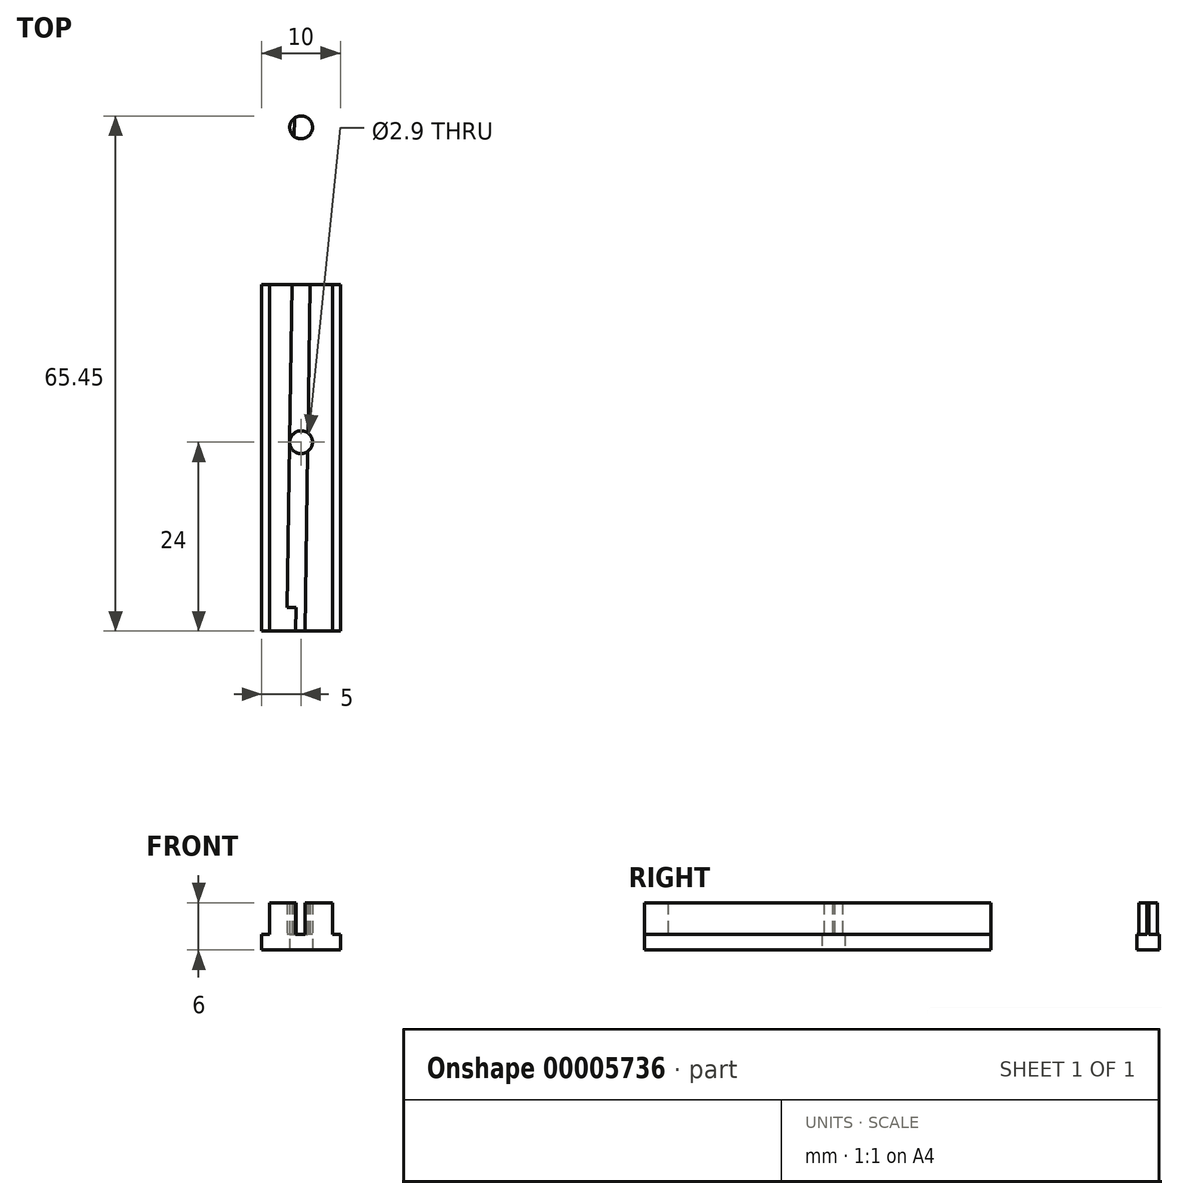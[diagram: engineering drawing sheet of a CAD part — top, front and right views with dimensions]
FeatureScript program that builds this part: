
annotation { "Feature Type Name" : "Feature", "Feature Type Description" : "" }
export const myFeature = defineFeature(function(context is Context, id is Id, definition is map)
    precondition{}
    {
        {
            var Q0;
            Q0=qCreatedBy(makeId("Top.planeOp"),FACE);
            var sketch = newSketch(context, id + "F0", { "sketchPlane" : qUnion([Q0])});
            skLineSegment(sketch, "E0.bottom", {"start": v(-5, 44) * mm, "end": v(5, 44) * mm});
            skLineSegment(sketch, "E0.top", {"start": v(-5, -44) * mm, "end": v(5, -44) * mm});
            skLineSegment(sketch, "E0.left", {"start": v(-5, 44) * mm, "end": v(-5, -44) * mm});
            skLineSegment(sketch, "E0.right", {"start": v(5, 44) * mm, "end": v(5, -44) * mm});
            skPoint(sketch, "E0.middle", {"position": v(0, 0) * mm});
            skLineSegment(sketch, "E1", {"start": v(0, 44) * mm, "end": v(0, -44) * mm, "construction": true});
            skLineSegment(sketch, "E2", {"start": v(1.8, 44) * mm, "end": v(0.5, -44) * mm});
            skLineSegment(sketch, "E3", {"start": v(-0.5, 44) * mm, "end": v(-1.8, -44) * mm});
            skLineSegment(sketch, "E4", {"start": v(0.7, 44) * mm, "end": v(0.66, 41) * mm});
            skLineSegment(sketch, "E5", {"start": v(0.66, 41) * mm, "end": v(1.76, 40.98) * mm});
            skLineSegment(sketch, "E6.1.0", {"start": v(-0.7, -44) * mm, "end": v(-0.66, -41) * mm});
            skLineSegment(sketch, "E6.1.1", {"start": v(-0.66, -41) * mm, "end": v(-1.76, -40.98) * mm});
            skLineSegment(sketch, "E7", {"start": v(4, 44) * mm, "end": v(4, -44) * mm});
            skLineSegment(sketch, "E8.MirrorCS", {"start": v(-4, 44) * mm, "end": v(-4, -44) * mm});
            skLineSegment(sketch, "E9.bottom", {"start": v(-4, 16.82) * mm, "end": v(4, 16.82) * mm});
            skLineSegment(sketch, "E9.top", {"start": v(-4, -16.82) * mm, "end": v(4, -16.82) * mm});
            skLineSegment(sketch, "E9.left", {"start": v(-4, 16.82) * mm, "end": v(-4, -16.82) * mm});
            skLineSegment(sketch, "E9.right", {"start": v(4, 16.82) * mm, "end": v(4, -16.82) * mm});
            skSolve(sketch);
        }
        {
            var Q0;
            {var subQ4=sQuery(id+"F0.wireOp",EDGE,"E0.left");Q0=makeQuery(id+"F0.imprint","IMPRINT",FACE,{"disambiguationData":[TD([[makeQuery(id+"F0.imprint","IMPRINT",EDGE,{"derivedFrom":subQ4}),1.0]])]});}
            var Q1;
            {var subQ4=sQuery(id+"F0.wireOp",EDGE,"E0.right");Q1=makeQuery(id+"F0.imprint","IMPRINT",FACE,{"disambiguationData":[TD([[makeQuery(id+"F0.imprint","IMPRINT",EDGE,{"derivedFrom":subQ4}),-1.0]])]});}
            var Q2;
            {var subQ3=sQuery(id+"F0.wireOp",EDGE,"E6.1.0");Q2=makeQuery(id+"F0.imprint","IMPRINT",FACE,{"disambiguationData":[TD([[makeQuery(id+"F0.imprint","IMPRINT",EDGE,{"derivedFrom":subQ3}),1.0]])]});}
            var Q3;
            {var subQ3=sQuery(id+"F0.wireOp",EDGE,"E4");Q3=makeQuery(id+"F0.imprint","IMPRINT",FACE,{"disambiguationData":[TD([[makeQuery(id+"F0.imprint","IMPRINT",EDGE,{"derivedFrom":subQ3}),1.0]])]});}
            var Q4;
            {var subQ6=sQuery(id+"F0.wireOp",EDGE,"E7");Q4=makeQuery(id+"F0.imprint","IMPRINT",FACE,{"disambiguationData":[TD([[makeQuery(id+"F0.imprint","IMPRINT",EDGE,{"derivedFrom":subQ6}),-1.0]])]});}
            var Q5;
            {var subQ3=sQuery(id+"F0.wireOp",EDGE,"E8.MirrorCS");Q5=makeQuery(id+"F0.imprint","IMPRINT",FACE,{"disambiguationData":[TD([[makeQuery(id+"F0.imprint","IMPRINT",EDGE,{"derivedFrom":subQ3}),1.0]])]});}
            var Q6;
            {var subQ1=sQuery(id+"F0.wireOp",EDGE,"E0.top");var subQ5=sQuery(id+"F0.wireOp",EDGE,"E3");var subQ7=makeQuery(id+"F0.imprint","INTERSECT",VERTEX,{"derivedFrom":[subQ1,subQ5]});Q6=makeQuery(id+"F0.imprint","IMPRINT",FACE,{"disambiguationData":[TD([[makeQuery(id+"F0.imprint","IMPRINT",EDGE,{"disambiguationData":[TD([[subQ7,1.0]])],"derivedFrom":subQ1}),1.0]])]});}
            var Q7;
            {var subQ5=sQuery(id+"F0.wireOp",EDGE,"E9.left");Q7=makeQuery(id+"F0.imprint","IMPRINT",FACE,{"disambiguationData":[TD([[makeQuery(id+"F0.imprint","IMPRINT",EDGE,{"derivedFrom":subQ5}),1.0]])]});}
            var Q8;
            {var subQ0=sQuery(id+"F0.wireOp",EDGE,"E9.bottom");var subQ1=sQuery(id+"F0.wireOp",EDGE,"E2");var subQ2=makeQuery(id+"F0.imprint","INTERSECT",VERTEX,{"derivedFrom":[subQ1,subQ0]});Q8=makeQuery(id+"F0.imprint","IMPRINT",FACE,{"disambiguationData":[TD([[makeQuery(id+"F0.imprint","IMPRINT",EDGE,{"disambiguationData":[TD([[subQ2,-1.0]])],"derivedFrom":subQ1}),-1.0]])]});}
            var Q9;
            {var subQ5=sQuery(id+"F0.wireOp",EDGE,"E9.right");Q9=makeQuery(id+"F0.imprint","IMPRINT",FACE,{"disambiguationData":[TD([[makeQuery(id+"F0.imprint","IMPRINT",EDGE,{"derivedFrom":subQ5}),-1.0]])]});}
            var Q10;
            {var subQ1=sQuery(id+"F0.wireOp",EDGE,"E0.bottom");var subQ5=sQuery(id+"F0.wireOp",EDGE,"E2");var subQ8=makeQuery(id+"F0.imprint","INTERSECT",VERTEX,{"derivedFrom":[subQ1,subQ5]});Q10=makeQuery(id+"F0.imprint","IMPRINT",FACE,{"disambiguationData":[TD([[makeQuery(id+"F0.imprint","IMPRINT",EDGE,{"disambiguationData":[TD([[subQ8,-1.0]])],"derivedFrom":subQ1}),-1.0]])]});}
            var Q11;
            {var subQ0=sQuery(id+"F0.wireOp",EDGE,"E4");Q11=makeQuery(id+"F0.imprint","IMPRINT",FACE,{"disambiguationData":[TD([[makeQuery(id+"F0.imprint","IMPRINT",EDGE,{"derivedFrom":subQ0}),-1.0]])]});}
            var Q12;
            {var subQ8=sQuery(id+"F0.wireOp",EDGE,"E6.1.0");Q12=makeQuery(id+"F0.imprint","IMPRINT",FACE,{"disambiguationData":[TD([[makeQuery(id+"F0.imprint","IMPRINT",EDGE,{"derivedFrom":subQ8}),-1.0]])]});}
            extrude(context, id + "F1", {"entities" : qUnion([Q0, Q1, Q2, Q3, Q4, Q5, Q6, Q7, Q8, Q9, Q10, Q11, Q12]), "oppositeDirection" : true, "depth" : 2 * mm});
        }
        {
            var Q0;
            {var subQ3=sQuery(id+"F0.wireOp",EDGE,"E8.MirrorCS");Q0=makeQuery(id+"F0.imprint","IMPRINT",FACE,{"disambiguationData":[TD([[makeQuery(id+"F0.imprint","IMPRINT",EDGE,{"derivedFrom":subQ3}),1.0]])]});}
            var Q1;
            {var subQ3=sQuery(id+"F0.wireOp",EDGE,"E6.1.0");Q1=makeQuery(id+"F0.imprint","IMPRINT",FACE,{"disambiguationData":[TD([[makeQuery(id+"F0.imprint","IMPRINT",EDGE,{"derivedFrom":subQ3}),1.0]])]});}
            var Q2;
            {var subQ6=sQuery(id+"F0.wireOp",EDGE,"E7");Q2=makeQuery(id+"F0.imprint","IMPRINT",FACE,{"disambiguationData":[TD([[makeQuery(id+"F0.imprint","IMPRINT",EDGE,{"derivedFrom":subQ6}),-1.0]])]});}
            var Q3;
            {var subQ3=sQuery(id+"F0.wireOp",EDGE,"E4");Q3=makeQuery(id+"F0.imprint","IMPRINT",FACE,{"disambiguationData":[TD([[makeQuery(id+"F0.imprint","IMPRINT",EDGE,{"derivedFrom":subQ3}),1.0]])]});}
            var Q4;
            {var subQ1=sQuery(id+"F0.wireOp",EDGE,"E0.top");var subQ5=sQuery(id+"F0.wireOp",EDGE,"E3");var subQ7=makeQuery(id+"F0.imprint","INTERSECT",VERTEX,{"derivedFrom":[subQ1,subQ5]});Q4=makeQuery(id+"F0.imprint","IMPRINT",FACE,{"disambiguationData":[TD([[makeQuery(id+"F0.imprint","IMPRINT",EDGE,{"disambiguationData":[TD([[subQ7,1.0]])],"derivedFrom":subQ1}),1.0]])]});}
            var Q5;
            {var subQ1=sQuery(id+"F0.wireOp",EDGE,"E0.bottom");var subQ5=sQuery(id+"F0.wireOp",EDGE,"E2");var subQ8=makeQuery(id+"F0.imprint","INTERSECT",VERTEX,{"derivedFrom":[subQ1,subQ5]});Q5=makeQuery(id+"F0.imprint","IMPRINT",FACE,{"disambiguationData":[TD([[makeQuery(id+"F0.imprint","IMPRINT",EDGE,{"disambiguationData":[TD([[subQ8,-1.0]])],"derivedFrom":subQ1}),-1.0]])]});}
            extrude(context, id + "F2", {"entities" : qUnion([Q0, Q1, Q2, Q3, Q4, Q5]), "operationType" : NewBodyOperationType.ADD, "depth" : 4 * mm});
        }
        {
            var Q0;
            Q0=makeQuery(id+"F1.opExtrude","CAP_FACE",FACE,{"disambiguationData":[OSD([sQuery(id+"F0.wireOp",EDGE,"E0.bottom"),sQuery(id+"F0.wireOp",EDGE,"E0.top"),sQuery(id+"F0.wireOp",EDGE,"E0.left"),sQuery(id+"F0.wireOp",EDGE,"E0.right")])],"isStart":false});
            var sketch = newSketch(context, id + "F3", { "sketchPlane" : qUnion([Q0])});
            skCircle(sketch, "E10", {"center": v(0, 20) * mm, "radius": 1.45 * mm});
            skLineSegment(sketch, "E11", {"start": v(5, 0) * mm, "end": v(-5, 0) * mm});
            skCircle(sketch, "E12.MirrorC", {"center": v(0, -20) * mm, "radius": 1.45 * mm});
            skSolve(sketch);
        }
        {
            var Q0;
            Q0=makeQuery(id+"F3.imprint","IMPRINT",FACE,{"disambiguationData":[TD([[makeQuery(id+"F3.imprint","IMPRINT",EDGE,{"derivedFrom":sQuery(id+"F3.wireOp",EDGE,"E10")}),1.0]])]});
            var Q1;
            Q1=makeQuery(id+"F3.imprint","IMPRINT",FACE,{"disambiguationData":[TD([[makeQuery(id+"F3.imprint","IMPRINT",EDGE,{"derivedFrom":sQuery(id+"F3.wireOp",EDGE,"E12.MirrorC")}),-1.0]])]});
            extrude(context, id + "F4", {"entities" : qUnion([Q0, Q1]), "operationType" : NewBodyOperationType.REMOVE, "oppositeDirection" : true, "depth" : 25 * mm});
        }
    });
